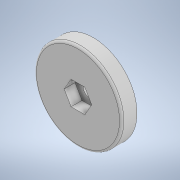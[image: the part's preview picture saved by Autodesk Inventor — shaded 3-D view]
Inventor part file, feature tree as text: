
AUTODESK INVENTOR PART (.ipt)
format: ipt  version: 2020 (Build 240168000, 168)  size: 163,328 bytes
history: native  units: mm
features: sketch x3, extrude x3, other x2, revolve x1, fillet x1
ambient origin geometry x8: Origin, YZ Plane, XZ Plane, XY Plane, X Axis, Y Axis, Z Axis, Center Point
bodies: Body1 (feature_tree)
feature tree (10):
  other  "Твердое тело1"
  sketch  "Эскиз1"
  revolve  "Вращение1"
  other  "РабПлоскость2"
  sketch  "Эскиз4"
  extrude  "Выдавливание5"  Depth=20.0mm
  extrude  "Выдавливание6"  Depth=3.5mm
  fillet  "Сопряжение1"  Radius=5.0mm
  extrude  "Выдавливание7"  Depth=2.2mm
  sketch  "Эскиз5"
